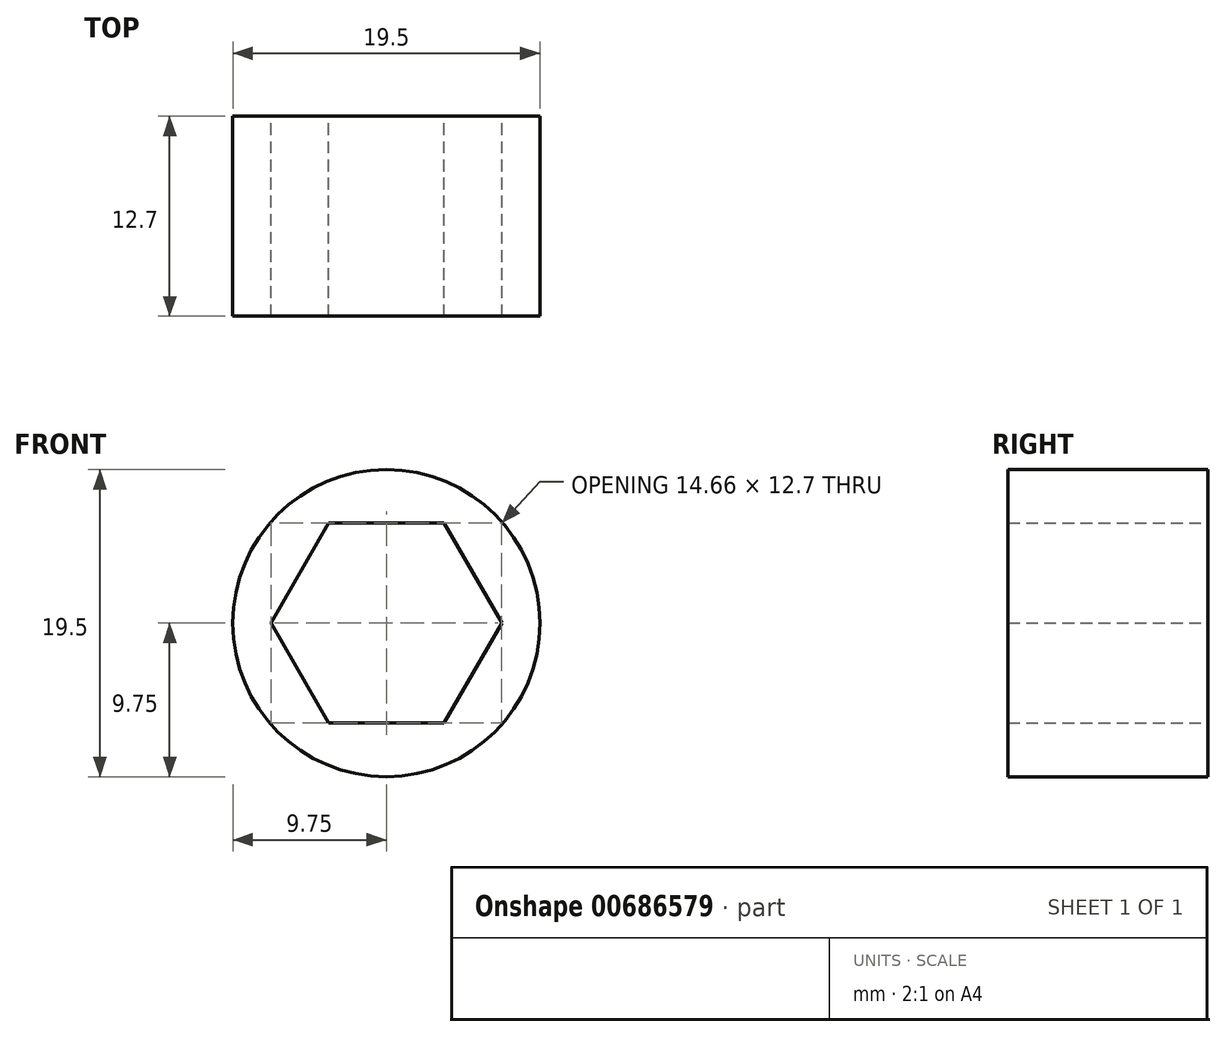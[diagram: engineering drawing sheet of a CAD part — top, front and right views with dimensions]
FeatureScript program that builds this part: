
annotation { "Feature Type Name" : "Feature", "Feature Type Description" : "" }
export const myFeature = defineFeature(function(context is Context, id is Id, definition is map)
    precondition{}
    {
        {
            var Q0;
            Q0=qCreatedBy(makeId("Front.planeOp"),FACE);
            var sketch = newSketch(context, id + "F0", { "sketchPlane" : qUnion([Q0])});
            skCircle(sketch, "E0", {"center": v(0, 0) * mm, "radius": 9.75 * mm});
            skCircle(sketch, "E1.cCircle", {"center": v(0, 0) * mm, "radius": 6.35 * mm, "construction": true});
            skLineSegment(sketch, "E1.0", {"start": v(-3.67, 6.35) * mm, "end": v(3.67, 6.35) * mm});
            skLineSegment(sketch, "E1.1", {"start": v(3.67, 6.35) * mm, "end": v(7.33, 0) * mm});
            skLineSegment(sketch, "E1.2", {"start": v(7.33, 0) * mm, "end": v(3.67, -6.35) * mm});
            skLineSegment(sketch, "E1.3", {"start": v(3.67, -6.35) * mm, "end": v(-3.67, -6.35) * mm});
            skLineSegment(sketch, "E1.4", {"start": v(-3.67, -6.35) * mm, "end": v(-7.33, 0) * mm});
            skLineSegment(sketch, "E1.5", {"start": v(-7.33, 0) * mm, "end": v(-3.67, 6.35) * mm});
            skPoint(sketch, "E1.0.midPoint", {"position": v(0, 6.35) * mm});
            skSolve(sketch);
        }
        {
            var Q0;
            Q0=makeQuery(id+"F0.imprint","IMPRINT",FACE,{"disambiguationData":[TD([[makeQuery(id+"F0.imprint","IMPRINT",EDGE,{"derivedFrom":sQuery(id+"F0.wireOp",EDGE,"E0")}),1.0]])]});
            extrude(context, id + "F1", {"entities" : qUnion([Q0]), "depth" : 12.7 * mm, "offsetDistance" : 25.4 * mm});
        }
    });
